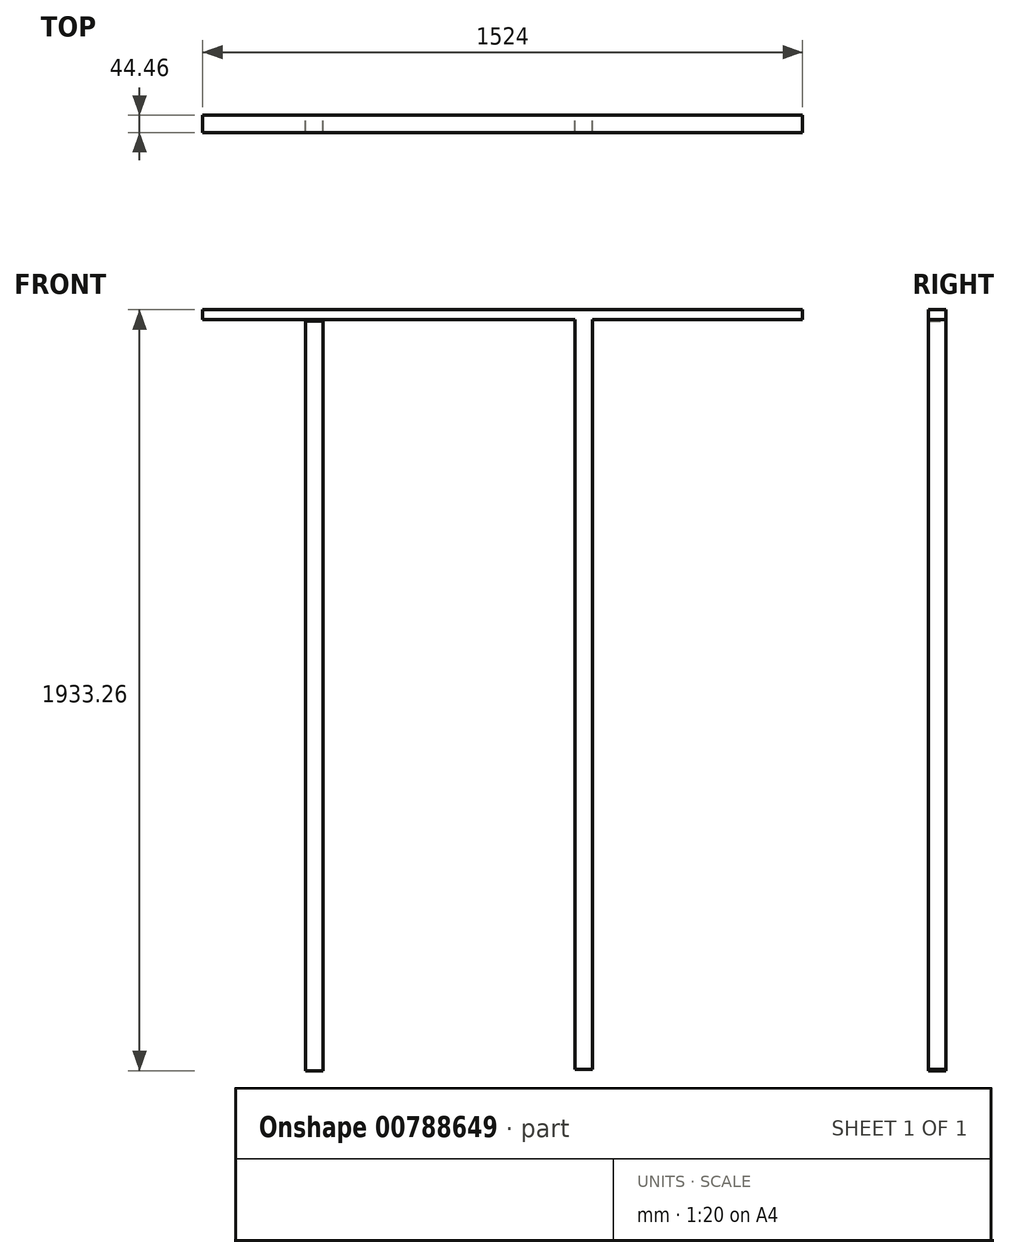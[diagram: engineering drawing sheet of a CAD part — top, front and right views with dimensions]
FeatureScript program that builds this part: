
annotation { "Feature Type Name" : "Feature", "Feature Type Description" : "" }
export const myFeature = defineFeature(function(context is Context, id is Id, definition is map)
    precondition{}
    {
        {
            var Q0;
            Q0=qCreatedBy(makeId("Front.planeOp"),FACE);
            var sketch = newSketch(context, id + "F0", { "sketchPlane" : qUnion([Q0])});
            skLineSegment(sketch, "E0.bottom", {"start": v(-765.15, 43.54) * mm, "end": v(758.85, 43.54) * mm});
            skLineSegment(sketch, "E0.top", {"start": v(-765.15, 18.25) * mm, "end": v(758.85, 18.25) * mm});
            skLineSegment(sketch, "E0.left", {"start": v(-765.15, 43.54) * mm, "end": v(-765.15, 18.25) * mm});
            skLineSegment(sketch, "E0.right", {"start": v(758.85, 43.54) * mm, "end": v(758.85, 18.25) * mm});
            skLineSegment(sketch, "E1.bottom", {"start": v(-503.3, 15.28) * mm, "end": v(-458.85, 15.28) * mm});
            skLineSegment(sketch, "E1.top", {"start": v(-503.3, -1889.72) * mm, "end": v(-458.85, -1889.72) * mm});
            skLineSegment(sketch, "E1.left", {"start": v(-503.3, 15.28) * mm, "end": v(-503.3, -1889.72) * mm});
            skLineSegment(sketch, "E1.right", {"start": v(-458.85, 15.28) * mm, "end": v(-458.85, -1889.72) * mm});
            skLineSegment(sketch, "E2.bottom", {"start": v(180.68, 18.25) * mm, "end": v(225.13, 18.25) * mm});
            skLineSegment(sketch, "E2.top", {"start": v(180.68, -1886.75) * mm, "end": v(225.13, -1886.75) * mm});
            skLineSegment(sketch, "E2.left", {"start": v(180.68, 18.25) * mm, "end": v(180.68, -1886.75) * mm});
            skLineSegment(sketch, "E2.right", {"start": v(225.13, 18.25) * mm, "end": v(225.13, -1886.75) * mm});
            skLineSegment(sketch, "E3", {"start": v(-458.85, -632.67) * mm, "end": v(180.68, 18.25) * mm});
            skSolve(sketch);
        }
        {
            var Q0;
            Q0=makeQuery(id+"F0.imprint","IMPRINT",FACE,{"disambiguationData":[TD([[makeQuery(id+"F0.imprint","IMPRINT",EDGE,{"derivedFrom":sQuery(id+"F0.wireOp",EDGE,"E2.top")}),1.0]])]});
            var Q1;
            Q1=makeQuery(id+"F0.imprint","IMPRINT",FACE,{"disambiguationData":[TD([[makeQuery(id+"F0.imprint","IMPRINT",EDGE,{"derivedFrom":sQuery(id+"F0.wireOp",EDGE,"E0.bottom")}),-1.0]])]});
            var Q2;
            {var subQ3=sQuery(id+"F0.wireOp",EDGE,"E1.bottom");Q2=makeQuery(id+"F0.imprint","IMPRINT",FACE,{"disambiguationData":[TD([[makeQuery(id+"F0.imprint","IMPRINT",EDGE,{"derivedFrom":subQ3}),-1.0]])]});}
            var Q3;
            Q3=sQuery(id+"F0.wireOp",EDGE,"E3");
            extrude(context, id + "F1", {"entities" : qUnion([Q0, Q1, Q2]), "surfaceOperationType" : NewSurfaceOperationType.ADD, "surfaceEntities" : qUnion([Q3]), "endBound" : BoundingType.SYMMETRIC, "depth" : 44.45 * mm, "offsetDistance" : 25.4 * mm});
        }
    });
